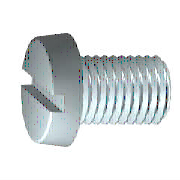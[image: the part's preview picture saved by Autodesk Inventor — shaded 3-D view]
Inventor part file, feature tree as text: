
AUTODESK INVENTOR PART (.ipt)
format: ipt  version: 2019.2 (Build 232265000, 265)  size: 180,224 bytes
history: native  units: mm (DEFAULTED — no unit token found)
features: sketch x2, other x1, extrude x1, plane x1
ambient origin geometry x7: Origin, YZ Plane, XZ Plane, X Axis, Y Axis, Z Axis, Center Point
bodies: Solid1 (feature_tree)
feature tree (5):
  other  "Körper"
  sketch  "Skizze2"  dims[d2=0.24548mm d3=1.3mm d4=2.0mm d5=1.783494mm d8=90.0deg d7=0.0mm d9=3.8mm d10=0.872665mm d11=0.5mm d12=3.8mm d14=0.1mm d15=11.2mm d16=0.0mm d17=0.216505mm d18=0.24548mm d19=0.6mm d20=0.0mm d36=45.0deg d37=0.0mm d39=0.0mm]
  extrude  "Loch"  Depth=11.2mm
  plane  "Work Plane1"
  sketch  "Skizze1"  dims[d0=12.0mm d1=11.2mm]
